FCSTD DOCUMENT  (FreeCAD 0.18R16093 (Git))
Label: couplerCap_big
License: All rights reserved
LicenseURL: http://en.wikipedia.org/wiki/All_rights_reserved
objects: Sketcher::SketchObject×1, PartDesign::Body×1
note: 2 computed .brp shape members not serialized (recipe doc carries the construction recipe); baked Part::Feature solids carry a one-line shape summary decoded from their .brp

FEATURE [Sketcher::SketchObject] Sketch
  MapMode = 5
  Support = -> [XY_Plane]
  sketch-geometry (4):
    g0: Circle CenterX=0 CenterY=0 CenterZ=0 NormalX=0 NormalY=0 NormalZ=1 AngleXU=0 Radius=32.55
    g1: Circle CenterX=-12 CenterY=6.89752 CenterZ=0 NormalX=0 NormalY=0 NormalZ=1 AngleXU=0 Radius=2
    g2: Circle CenterX=12 CenterY=6.89752 CenterZ=0 NormalX=0 NormalY=0 NormalZ=1 AngleXU=0 Radius=2
    g3: Circle CenterX=0 CenterY=0 CenterZ=0 NormalX=0 NormalY=0 NormalZ=1 AngleXU=0 Radius=3
  constraints (9):
    c: Coincident(g0,g-1)
    c: Radius(g0) = 32.55
    c: Horizontal(g1,g2)
    c: Equal(g2,g1)
    c: Radius(g1) = 2
    c: DistanceX(g1,g0) = 12
    c: DistanceX(g0,g2) = 12
    c: Coincident(g3,g0)
    c: Radius(g3) = 3
FEATURE [PartDesign::Body] Body
  Group = -> [Sketch]
  Origin = -> Origin
